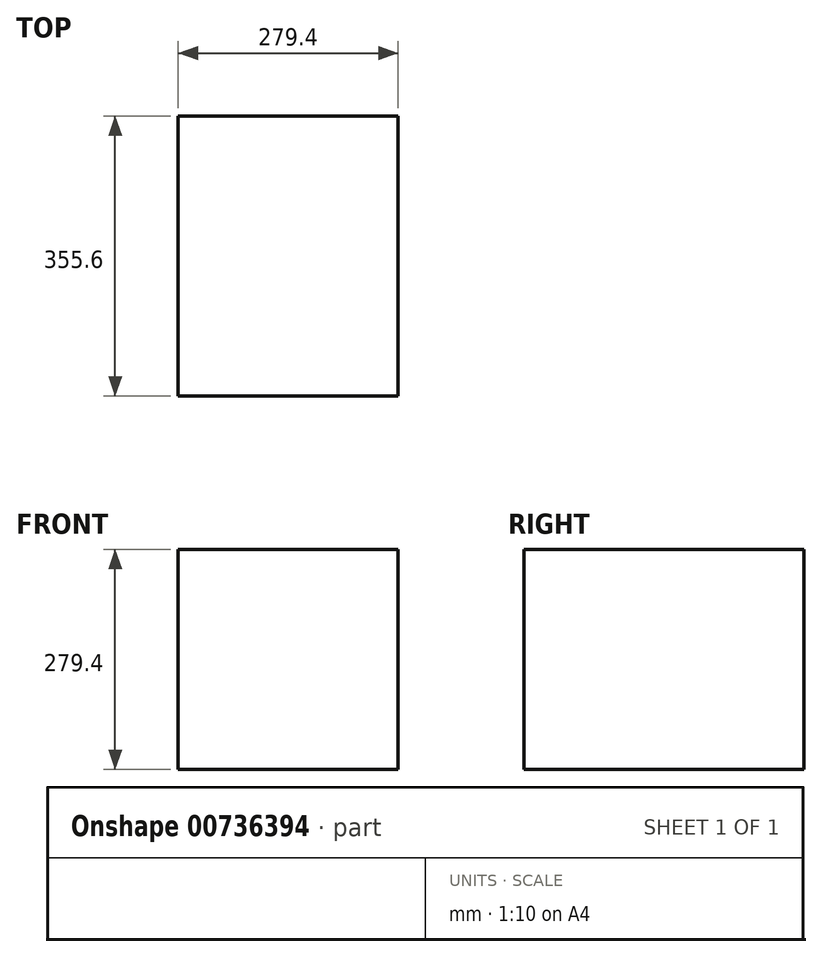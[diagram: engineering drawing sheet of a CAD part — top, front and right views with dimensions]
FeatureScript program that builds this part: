
annotation { "Feature Type Name" : "Feature", "Feature Type Description" : "" }
export const myFeature = defineFeature(function(context is Context, id is Id, definition is map)
    precondition{}
    {
        {
            var Q0;
            Q0=qCreatedBy(makeId("Front.planeOp"),FACE);
            var sketch = newSketch(context, id + "F0", { "sketchPlane" : qUnion([Q0])});
            skLineSegment(sketch, "E0.bottom", {"start": v(0, 0) * mm, "end": v(279.4, 0) * mm});
            skLineSegment(sketch, "E0.top", {"start": v(0, 279.4) * mm, "end": v(279.4, 279.4) * mm});
            skLineSegment(sketch, "E0.left", {"start": v(0, 0) * mm, "end": v(0, 279.4) * mm});
            skLineSegment(sketch, "E0.right", {"start": v(279.4, 0) * mm, "end": v(279.4, 279.4) * mm});
            skSolve(sketch);
        }
        {
            var Q0;
            Q0=makeQuery(id+"F0.imprint","IMPRINT",FACE,{"disambiguationData":[TD([[makeQuery(id+"F0.imprint","IMPRINT",EDGE,{"derivedFrom":sQuery(id+"F0.wireOp",EDGE,"E0.bottom")}),1.0]])]});
            extrude(context, id + "F1", {"entities" : qUnion([Q0]), "depth" : 355.6 * mm, "offsetDistance" : 25.4 * mm});
        }
    });
